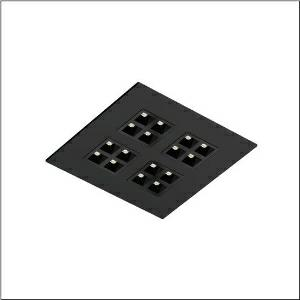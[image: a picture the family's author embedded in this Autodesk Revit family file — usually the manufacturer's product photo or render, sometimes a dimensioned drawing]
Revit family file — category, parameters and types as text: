
# Revit family: silica_r__31_square_51my6lds44ba_4de6
name_source: partatom
category: Lighting Fixtures
units: mm (PartAtom-declared; Revit-internal decimal feet)

## family parameters
Cut with Voids When Loaded = No
Host = Face
Light Source = No
Part Type = Normal
Room Calculation Point = No
Round Connector Dimension = Use Diameter
Shared = No

## types (1)
- --- (1 x LED, 6310 lm, 38.5 W, 4000K)
    Apparent Load = 39 VA
    CIE Flux Codes = 82 100 100 100 100
    Color Rendering = 80
    Color Temperature = 4000K
    Default Elevation = 1800 mm
    Description = Silica® 31 Square, office luminaire, primary light control with lens, of PMMA, primary anti-glare with reflector, of PC, black, light emission: direct distribution, primary light characteristic: symmetric, installation type: lay-in mounting, LED, rated luminous flux: 4.620lm, luminous efficacy: 167lm/W, light colour: 840, colour temperature: 4000K, control gear: DALI 2, Multilumen, with terminal, 5-pole, mains connection: 220..240V, AC, 50/60Hz, rated input power: 27.6W, luminaire housing, of sheet steel, coated, jet black (RAL 9005), module: M600, length: 595mm, width: 595mm, height: 43mm, protection rating (complete): IP20, insulation class (complete): insulation class II (safety insulation), certification: CE, impact resistance: IK03, permissible operating ambient temperature: -20..+35°C, standard: EN 50419, packaging unit: 1 piece
    Height = 0 mm  [stored 0 ft]
    Lamp = 1 x LED
    Lamp Light Flux = 6310 lm
    Lamp Power = 38.5 W
    Lamp count = 1
    Length = 595 mm
    Luminous efficacy = 164 lm/W
    Manufacturer = Siteco
    ModVariant = No
    Model = 51MY6LDS44BA
    Mounting Place = Ceiling
    Mounting Type = Recessed
    Number of Poles = 1
    OnlyDefault = Yes
    Power Factor = 1
    Product Name = Silica® 31 Square
    Product group = office luminaire | ceiling recessed
    ProductGroupID = 401
    Protection Class = Protection class II
    Protection Degree = IP 20
    RLX_Detail_Level = 1
    RLX_Emergency_Light_Flux = 0 lm
    RLX_Emergency_Type = 0
    RLX_Emergency_Type_DB = No
    RlxData = <blob elided: 35481 chars, md5=992a950e>
    Socket = socket
    Standby Power = 0 W
    System Light Flux = 6310 lm
    System Power = 39 W
    Type Comments = factory setting: luminous flux: 100 % | (OFF | OFF | OFF | OFF) | 1050 mA
    Type Image = l_1313660.jpg
    URL = http://relux.com
    VarID = @adj_036184
    Voltage = 0 V
    Weight = 0.00 kg
    Width = 595 mm

note: [stored X ft] marks values corroborated as IEEE doubles in the binary element streams (Revit-internal decimal feet)

## geometry (parser evidence)
native form markers: Blend x4, Sweep x11
no freeform markers — native parametric forms only
